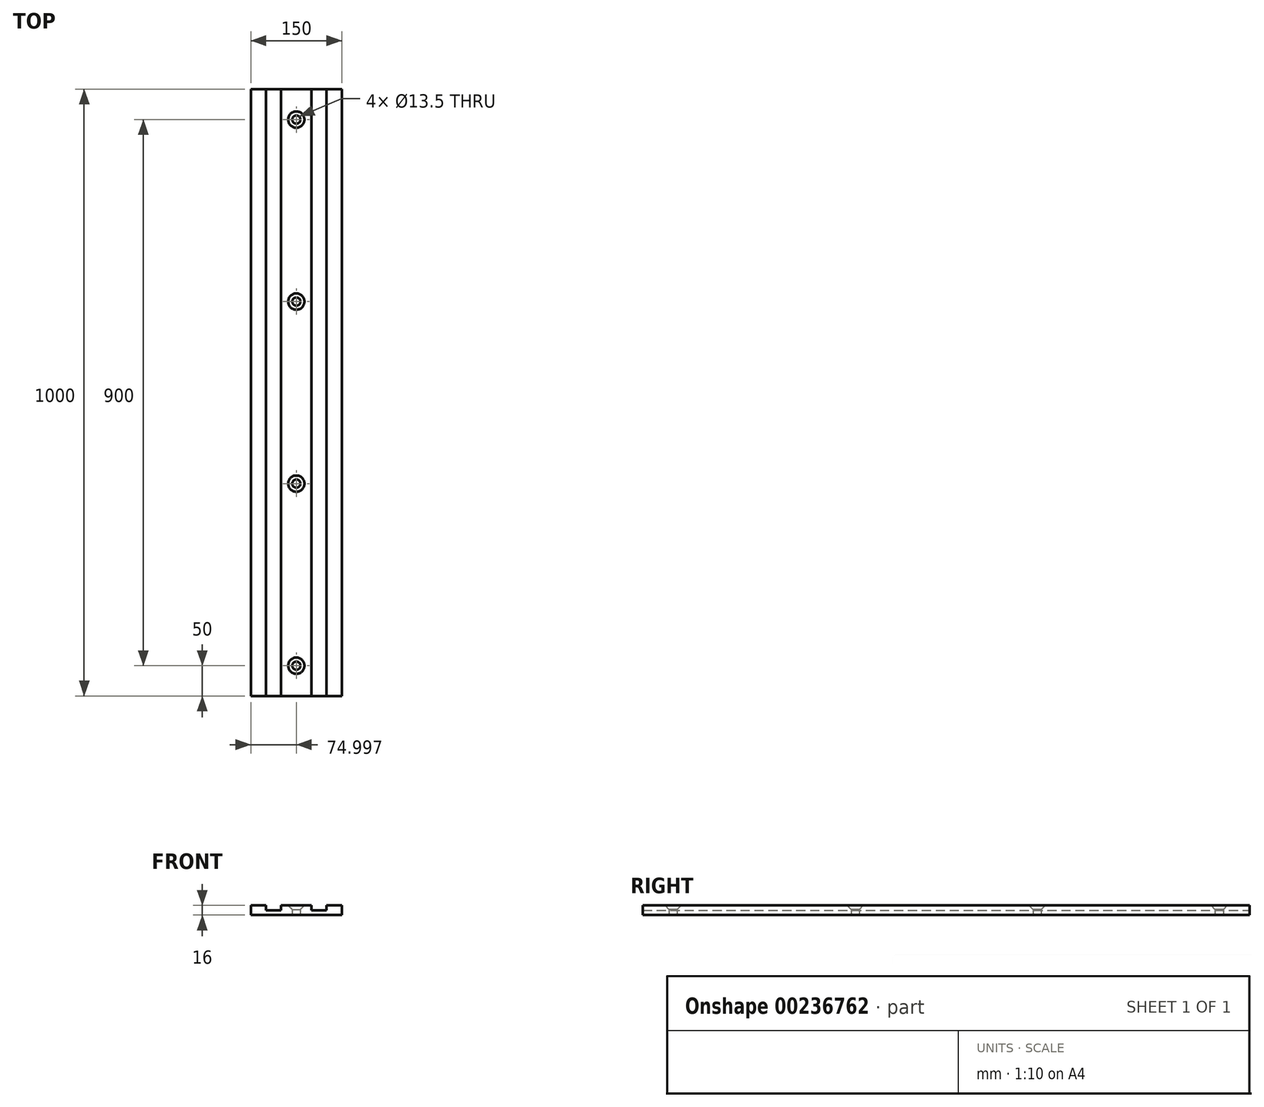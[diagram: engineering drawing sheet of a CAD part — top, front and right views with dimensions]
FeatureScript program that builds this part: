
annotation { "Feature Type Name" : "Feature", "Feature Type Description" : "" }
export const myFeature = defineFeature(function(context is Context, id is Id, definition is map)
    precondition{}
    {
        {
            var Q0;
            Q0=qCreatedBy(makeId("Front.planeOp"),FACE);
            var sketch = newSketch(context, id + "F0", { "sketchPlane" : qUnion([Q0])});
            skLineSegment(sketch, "E0", {"start": v(-32.8, 0) * mm, "end": v(-32.8, 16) * mm});
            skLineSegment(sketch, "E1", {"start": v(-32.8, 16) * mm, "end": v(-7.8, 16) * mm});
            skLineSegment(sketch, "E2", {"start": v(-7.8, 16) * mm, "end": v(-7.8, 8) * mm});
            skLineSegment(sketch, "E3", {"start": v(-7.8, 8) * mm, "end": v(17.2, 8) * mm});
            skLineSegment(sketch, "E4", {"start": v(17.2, 8) * mm, "end": v(17.2, 16) * mm});
            skLineSegment(sketch, "E5", {"start": v(17.2, 16) * mm, "end": v(67.2, 16) * mm});
            skLineSegment(sketch, "E6", {"start": v(42.2, 16) * mm, "end": v(67.2, 16) * mm});
            skLineSegment(sketch, "E7", {"start": v(117.2, 16) * mm, "end": v(117.2, 0) * mm});
            skLineSegment(sketch, "E8", {"start": v(117.2, 0) * mm, "end": v(-32.8, 0) * mm});
            skLineSegment(sketch, "E9", {"start": v(67.2, 16) * mm, "end": v(67.2, 8) * mm});
            skLineSegment(sketch, "E10", {"start": v(67.2, 8) * mm, "end": v(92.2, 8) * mm});
            skLineSegment(sketch, "E11", {"start": v(92.2, 8) * mm, "end": v(92.2, 16) * mm});
            skLineSegment(sketch, "E12.trimOffspring", {"start": v(92.2, 16) * mm, "end": v(117.2, 16) * mm});
            skSolve(sketch);
        }
        {
            var Q0;
            Q0 = qSketchRegion(id + "F0", true);
            extrude(context, id + "F1", {"entities" : qUnion([Q0]), "depth" : 1000 * mm, "offsetDistance" : 25 * mm});
        }
        {
            var Q0;
            Q0=makeQuery(id+"F1.opExtrude","SWEPT_FACE",FACE,{"disambiguationData":[OSD([sQuery(id+"F0.wireOp",EDGE,"E5"),sQuery(id+"F0.wireOp",EDGE,"E6")])]});
            var sketch = newSketch(context, id + "F2", { "sketchPlane" : qUnion([Q0])});
            skPoint(sketch, "E13", {"position": v(42.2, -950) * mm});
            skPoint(sketch, "E13.positionSnap0", {"position": v(42.2, -1000) * mm});
            skPoint(sketch, "E14", {"position": v(42.2, -650) * mm});
            skPoint(sketch, "E15", {"position": v(42.2, -350) * mm});
            skPoint(sketch, "E16", {"position": v(42.2, -50) * mm});
            skSolve(sketch);
        }
        {
            var Q0;
            Q0=sQuery(id+"F2.wireOp",VERTEX,"E16");
            var Q1;
            Q1=sQuery(id+"F2.wireOp",VERTEX,"E15");
            var Q2;
            Q2=sQuery(id+"F2.wireOp",VERTEX,"E14");
            var Q3;
            Q3=sQuery(id+"F2.wireOp",VERTEX,"E13");
            var Q4;
            Q4=makeQuery(id+"F1.opExtrude","SWEPT_BODY",BODY,{"disambiguationData":[OSD([sQuery(id+"F0.wireOp",EDGE,"E0"),sQuery(id+"F0.wireOp",EDGE,"E1"),sQuery(id+"F0.wireOp",EDGE,"E2"),sQuery(id+"F0.wireOp",EDGE,"E3"),sQuery(id+"F0.wireOp",EDGE,"E4"),sQuery(id+"F0.wireOp",EDGE,"E5"),sQuery(id+"F0.wireOp",EDGE,"E6"),sQuery(id+"F0.wireOp",EDGE,"E7"),sQuery(id+"F0.wireOp",EDGE,"E8"),sQuery(id+"F0.wireOp",EDGE,"E9"),sQuery(id+"F0.wireOp",EDGE,"E10"),sQuery(id+"F0.wireOp",EDGE,"E11"),sQuery(id+"F0.wireOp",EDGE,"E12.trimOffspring")])]});
            hole(context, id + "F3", {"style" : HoleStyle.C_SINK, "endStyle" : HoleEndStyle.BLIND, "standardTappedOrClearance" : lookupTablePath({ "fit" : "Normal", "standard" : "ISO", "size" : "M12", "type" : "Clearance" }), "standardBlindInLast" : lookupTablePath({ "fit" : "Normal", "standard" : "ISO", "engagement" : "75%", "pitch" : "1.75 mm", "size" : "M12", "type" : "Clearance & tapped" }), "holeDiameter" : 13.5 * mm, "cSinkDiameter" : 26.88 * mm, "cSinkAngle" : 90 * degree, "majorDiameter" : 5 * mm, "holeDepth" : 16 * mm, "isTappedThrough" : true, "tappedDepth" : 31.25 * mm, "tapClearance" : 3, "startFromSketch" : true, "locations" : qUnion([Q0, Q1, Q2, Q3]), "scope" : qUnion([Q4])});
        }
    });
